# Revit family: Faucet-Bath_Filler-KALLISTA-One-P32364_1
name_source: partatom
category: Plumbing Fixtures
units: mm (PartAtom-declared; Revit-internal decimal feet)

## family parameters
Cut with Voids When Loaded = No
Host = Face
OmniClass Number = 23.31.11.00
OmniClass Title = Faucets
Part Type = Normal
Room Calculation Point = No
Round Connector Dimension = Use Diameter
Shared = No

## types (2) — shared parameters
ADA Compliant = No
Assembly Code = D2010
CW Connection = Yes
Cold Water Inlet = Cold Water Inlet
Date Modified = 02/14/2023
Default Elevation = 36"
Description = Freestanding Bath Faucet
Drain Included = No
Faucet Hole Spacing = 0"
Flow Rate = 8 GPM
HW Connection = Yes
Handle Clearance = 3 7/16"
Height = 37 7/8"
Hot Water Inlet = Hot Water Inlet
Length = 12 1/4"
Manufacturer = Kallista Co.
Master Format 2014 = 22 41 39
Master Format 2014 Name = Residential Faucets, Supplies, and Trim
Material = Solid Brass Construction
Pressure = 0.00 psi
Product Name = One
Spout Reach = 12 1/4"
Tempered Water Outlet = Tempered Water Outlet
URL = https://www.kallista.com
Vent Connection = No
Waste Connection = No
Waste Water Outlet = Waste Water Outlet
WaterSense Certified = No
Width = 4 3/4"

## per-type parameters (varying)
| type | Finish | Model | Secondary Finish | Type |
| AD, BAF-Brushed French Gold | Kallista-Metal-BAF-Brushed_French_Gold | P32364-AD-BAF | Kallista-Metal-AD-Nickel_Silver | 1 |
| ULB, SN-Polished Nickel | Kallista-Metal-SN-Polished_Nickel | P32364-ULB-SN | Kallista-Metal-ULB-Unlaquered_Brass | 2 |

## geometry (parser evidence)
native form markers: Sweep x6
no freeform markers — native parametric forms only
